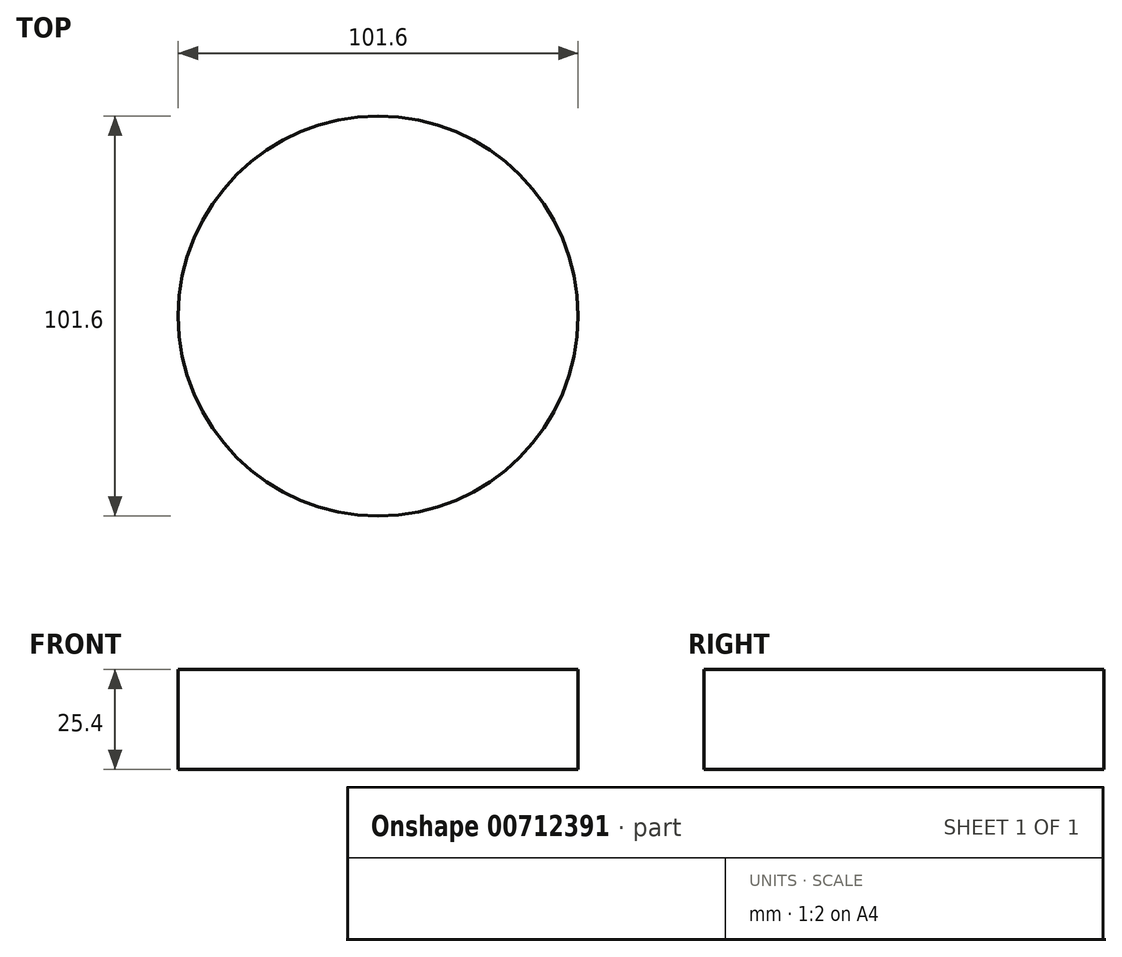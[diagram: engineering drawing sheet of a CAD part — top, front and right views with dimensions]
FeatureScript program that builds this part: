
annotation { "Feature Type Name" : "Feature", "Feature Type Description" : "" }
export const myFeature = defineFeature(function(context is Context, id is Id, definition is map)
    precondition{}
    {
        {
            var Q0;
            Q0=qCreatedBy(makeId("Top.planeOp"),FACE);
            var sketch = newSketch(context, id + "F0", { "sketchPlane" : qUnion([Q0])});
            skCircle(sketch, "E0", {"center": v(0, 0) * mm, "radius": 50.8 * mm});
            skSolve(sketch);
        }
        {
            var Q0;
            Q0 = qSketchRegion(id + "F0", true);
            extrude(context, id + "F1", {"entities" : qUnion([Q0]), "depth" : 25.4 * mm, "offsetDistance" : 25.4 * mm});
        }
        {
            var Q0;
            Q0 = qSketchRegion(id + "F0", true);
            extrude(context, id + "F2", {"entities" : qUnion([Q0]), "operationType" : NewBodyOperationType.ADD, "depth" : 25.4 * mm, "offsetDistance" : 25.4 * mm});
        }
        {
            var Q0;
            Q0 = qSketchRegion(id + "F0", true);
            extrude(context, id + "F3", {"entities" : qUnion([Q0]), "operationType" : NewBodyOperationType.ADD, "depth" : 4.2 * mm, "offsetDistance" : 25.4 * mm});
        }
        {
            var Q0;
            Q0=makeQuery(id+"F0.imprint","IMPRINT",FACE,{"disambiguationData":[TD([[makeQuery(id+"F0.imprint","IMPRINT",EDGE,{"derivedFrom":sQuery(id+"F0.wireOp",EDGE,"E0")}),1.0]])]});
            extrude(context, id + "F4", {"entities" : qUnion([Q0]), "operationType" : NewBodyOperationType.ADD, "depth" : 25.4 * mm, "offsetDistance" : 25.4 * mm});
        }
    });
